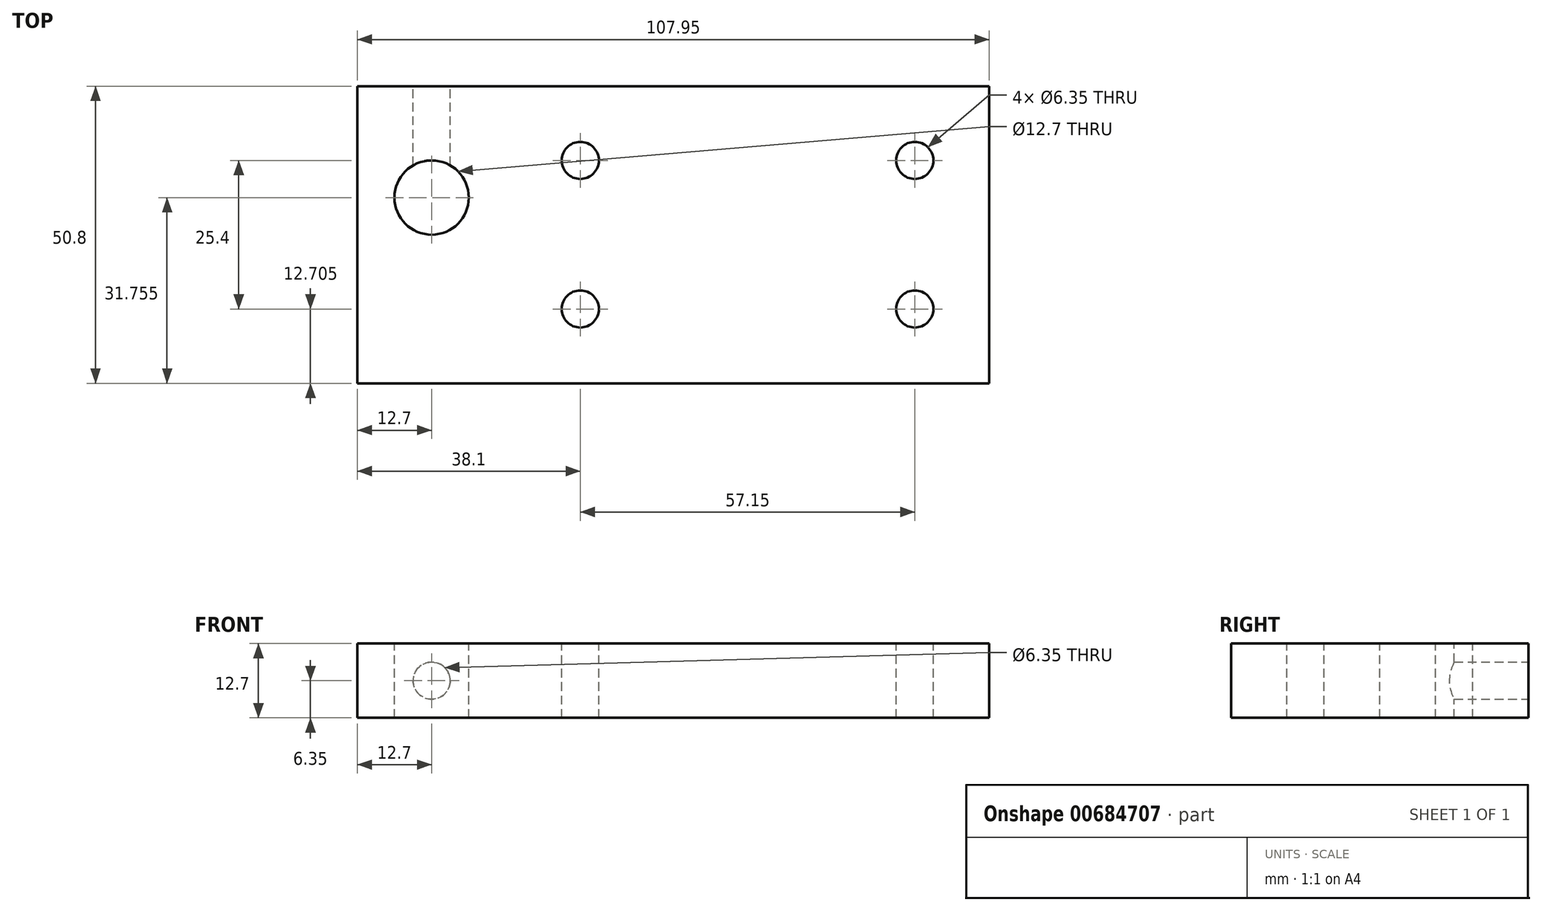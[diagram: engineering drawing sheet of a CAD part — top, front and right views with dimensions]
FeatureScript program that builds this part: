
annotation { "Feature Type Name" : "Feature", "Feature Type Description" : "" }
export const myFeature = defineFeature(function(context is Context, id is Id, definition is map)
    precondition{}
    {
        {
            var Q0;
            Q0=qCreatedBy(makeId("Top.planeOp"),FACE);
            var sketch = newSketch(context, id + "F0", { "sketchPlane" : qUnion([Q0])});
            skLineSegment(sketch, "E0", {"start": v(0, 0) * mm, "end": v(0, 16.54) * mm});
            skLineSegment(sketch, "E1", {"start": v(0, 16.54) * mm, "end": v(64.84, 16.54) * mm});
            skLineSegment(sketch, "E2", {"start": v(64.84, 16.54) * mm, "end": v(64.84, -34.26) * mm});
            skLineSegment(sketch, "E3", {"start": v(64.84, -34.26) * mm, "end": v(-43.11, -34.26) * mm});
            skLineSegment(sketch, "E4", {"start": v(-43.11, -34.26) * mm, "end": v(-43.11, 16.54) * mm});
            skLineSegment(sketch, "E5", {"start": v(-43.11, 16.54) * mm, "end": v(0, 16.54) * mm});
            skSolve(sketch);
        }
        {
            var Q0;
            Q0 = qSketchRegion(id + "F0", true);
            extrude(context, id + "F1", {"entities" : qUnion([Q0]), "depth" : 12.7 * mm, "offsetDistance" : 25.4 * mm});
        }
        {
            var Q0;
            Q0=makeQuery(id+"F1.opExtrude","CAP_FACE",FACE,{"disambiguationData":[OSD([sQuery(id+"F0.wireOp",EDGE,"E1"),sQuery(id+"F0.wireOp",EDGE,"E2"),sQuery(id+"F0.wireOp",EDGE,"E3"),sQuery(id+"F0.wireOp",EDGE,"E4"),sQuery(id+"F0.wireOp",EDGE,"E5")])],"isStart":false});
            var sketch = newSketch(context, id + "F2", { "sketchPlane" : qUnion([Q0])});
            skCircle(sketch, "E6", {"center": v(-5.01, -21.56) * mm, "radius": 3.18 * mm});
            skCircle(sketch, "E7", {"center": v(-5.01, 3.84) * mm, "radius": 3.18 * mm});
            skCircle(sketch, "E8", {"center": v(52.14, 3.84) * mm, "radius": 3.18 * mm});
            skCircle(sketch, "E9", {"center": v(52.14, -21.56) * mm, "radius": 3.18 * mm});
            skSolve(sketch);
        }
        {
            var Q0;
            Q0 = qSketchRegion(id + "F2", true);
            extrude(context, id + "F3", {"entities" : qUnion([Q0]), "operationType" : NewBodyOperationType.REMOVE, "oppositeDirection" : true, "depth" : 25.4 * mm, "offsetDistance" : 25.4 * mm});
        }
        {
            var Q0;
            Q0=makeQuery(id+"F1.opExtrude","CAP_FACE",FACE,{"disambiguationData":[OSD([sQuery(id+"F0.wireOp",EDGE,"E1"),sQuery(id+"F0.wireOp",EDGE,"E2"),sQuery(id+"F0.wireOp",EDGE,"E3"),sQuery(id+"F0.wireOp",EDGE,"E4"),sQuery(id+"F0.wireOp",EDGE,"E5")])],"isStart":false});
            var sketch = newSketch(context, id + "F4", { "sketchPlane" : qUnion([Q0])});
            skCircle(sketch, "E10", {"center": v(-30.41, -2.5) * mm, "radius": 6.35 * mm});
            skSolve(sketch);
        }
        {
            var Q0;
            Q0 = qSketchRegion(id + "F4", true);
            extrude(context, id + "F5", {"entities" : qUnion([Q0]), "operationType" : NewBodyOperationType.REMOVE, "oppositeDirection" : true, "depth" : 25.4 * mm, "offsetDistance" : 25.4 * mm});
        }
        {
            var Q0;
            Q0=makeQuery(id+"F1.opExtrude","SWEPT_FACE",FACE,{"disambiguationData":[OSD([sQuery(id+"F0.wireOp",EDGE,"E1"),sQuery(id+"F0.wireOp",EDGE,"E5")])]});
            var sketch = newSketch(context, id + "F6", { "sketchPlane" : qUnion([Q0])});
            skCircle(sketch, "E11", {"center": v(30.41, 6.35) * mm, "radius": 3.18 * mm});
            skSolve(sketch);
        }
        {
            var Q0;
            Q0 = qSketchRegion(id + "F6", true);
            extrude(context, id + "F7", {"entities" : qUnion([Q0]), "operationType" : NewBodyOperationType.REMOVE, "oppositeDirection" : true, "depth" : 19.05 * mm, "offsetDistance" : 25.4 * mm});
        }
    });
